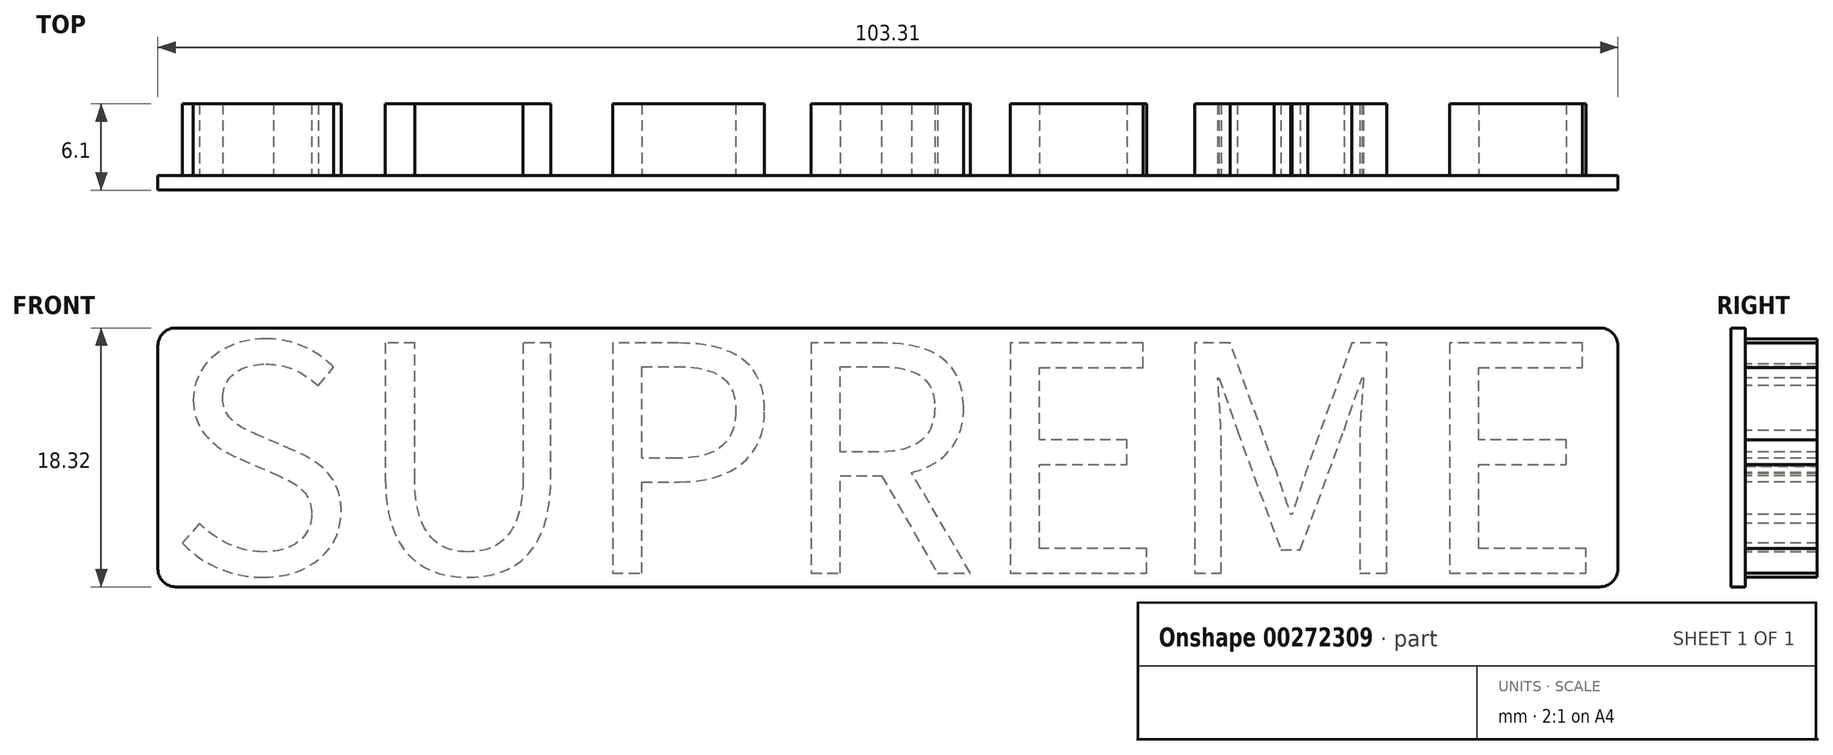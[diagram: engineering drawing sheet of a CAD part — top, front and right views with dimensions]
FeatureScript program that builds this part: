
annotation { "Feature Type Name" : "Feature", "Feature Type Description" : "" }
export const myFeature = defineFeature(function(context is Context, id is Id, definition is map)
    precondition{}
    {
        {
            var Q0;
            Q0=qCreatedBy(makeId("Front.planeOp"),FACE);
            var sketch = newSketch(context, id + "F0", { "sketchPlane" : qUnion([Q0])});
            skText(sketch, "E0", { "text": "SUPREME", "fontName": "NotoSansCJKkr-Regular.otf"});
            const initialGuessF0  = {"E0": [-0.0323, 0.0043, 1, 0, 0.01599]};
            skSetInitialGuess(sketch, initialGuessF0);
            skSolve(sketch);
        }
        {
            var Q0;
            Q0=qCreatedBy(makeId("Front.planeOp"),FACE);
            var sketch = newSketch(context, id + "F1", { "sketchPlane" : qUnion([Q0])});
            skLineSegment(sketch, "E1.bottom", {"start": v(-32.99, 21.65) * mm, "end": v(70.32, 21.65) * mm});
            skLineSegment(sketch, "E1.top", {"start": v(-32.99, 3.33) * mm, "end": v(70.32, 3.33) * mm});
            skLineSegment(sketch, "E1.left", {"start": v(-32.99, 21.65) * mm, "end": v(-32.99, 3.33) * mm});
            skLineSegment(sketch, "E1.right", {"start": v(70.32, 21.65) * mm, "end": v(70.32, 3.33) * mm});
            skSolve(sketch);
        }
        {
            var Q0;
            Q0 = qSketchRegion(id + "F1", true);
            extrude(context, id + "F2", {"entities" : qUnion([Q0]), "depth" : 1.02 * mm});
        }
        {
            var Q0;
            Q0 = qSketchRegion(id + "F0", true);
            extrude(context, id + "F3", {"entities" : qUnion([Q0]), "operationType" : NewBodyOperationType.REMOVE, "oppositeDirection" : true, "depth" : 5.08 * mm});
        }
        {
            var Q0;
            Q0 = qSketchRegion(id + "F0", true);
            extrude(context, id + "F4", {"entities" : qUnion([Q0]), "operationType" : NewBodyOperationType.ADD, "oppositeDirection" : true, "depth" : 5.08 * mm});
        }
        {
            var Q0;
            Q0=makeQuery(id+"F2.opExtrude","SWEPT_EDGE",EDGE,{"disambiguationData":[OSD([sQuery(id+"F1.wireOp",EDGE,"E1.bottom"),sQuery(id+"F1.wireOp",EDGE,"E1.right")])]});
            var Q1;
            Q1=makeQuery(id+"F2.opExtrude","SWEPT_EDGE",EDGE,{"disambiguationData":[OSD([sQuery(id+"F1.wireOp",EDGE,"E1.top"),sQuery(id+"F1.wireOp",EDGE,"E1.right")])]});
            var Q2;
            Q2=makeQuery(id+"F2.opExtrude","SWEPT_EDGE",EDGE,{"disambiguationData":[OSD([sQuery(id+"F1.wireOp",EDGE,"E1.bottom"),sQuery(id+"F1.wireOp",EDGE,"E1.left")])]});
            var Q3;
            Q3=makeQuery(id+"F2.opExtrude","SWEPT_EDGE",EDGE,{"disambiguationData":[OSD([sQuery(id+"F1.wireOp",EDGE,"E1.top"),sQuery(id+"F1.wireOp",EDGE,"E1.left")])]});
            fillet(context, id + "F5", {"entities" : qUnion([Q0, Q1, Q2, Q3]), "radius" : 1.27 * mm, "tangentPropagation" : true, "allowEdgeOverflow" : false});
        }
    });
